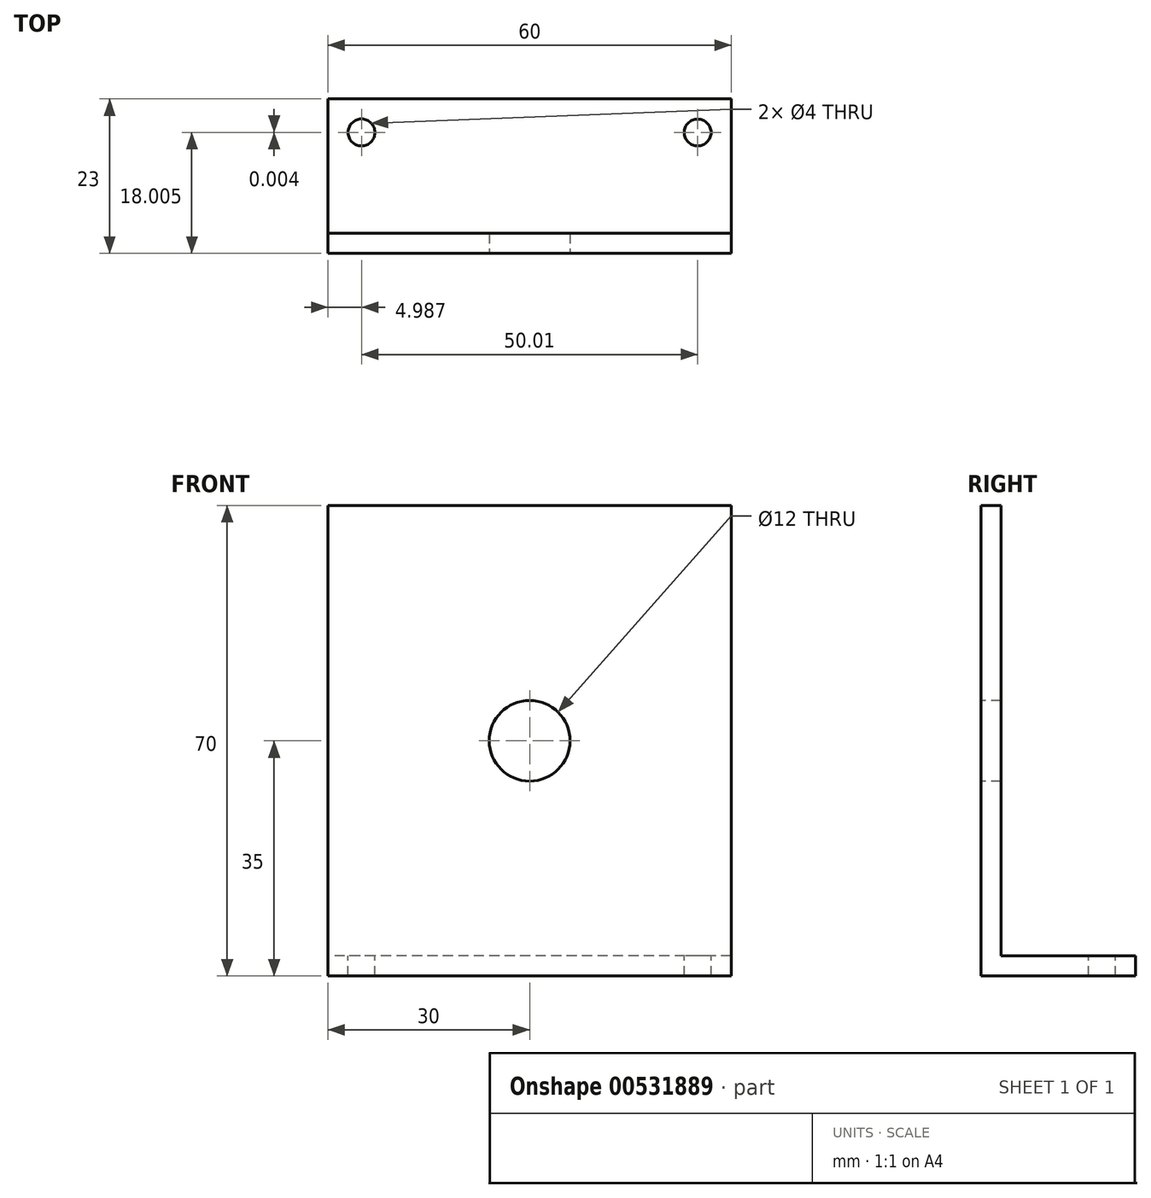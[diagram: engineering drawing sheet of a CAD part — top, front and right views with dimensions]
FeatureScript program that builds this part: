
annotation { "Feature Type Name" : "Feature", "Feature Type Description" : "" }
export const myFeature = defineFeature(function(context is Context, id is Id, definition is map)
    precondition{}
    {
        {
            var Q0;
            Q0=qCreatedBy(makeId("Front.planeOp"),FACE);
            var sketch = newSketch(context, id + "F0", { "sketchPlane" : qUnion([Q0])});
            skLineSegment(sketch, "E0.bottom", {"start": v(30, -35) * mm, "end": v(-30, -35) * mm});
            skLineSegment(sketch, "E0.top", {"start": v(30, 35) * mm, "end": v(-30, 35) * mm});
            skLineSegment(sketch, "E0.left", {"start": v(30, -35) * mm, "end": v(30, 35) * mm});
            skLineSegment(sketch, "E0.right", {"start": v(-30, -35) * mm, "end": v(-30, 35) * mm});
            skPoint(sketch, "E0.middle", {"position": v(0, 0) * mm});
            skSolve(sketch);
        }
        {
            var Q0;
            Q0=makeQuery(id+"F0.imprint","IMPRINT",FACE,{"disambiguationData":[TD([[makeQuery(id+"F0.imprint","IMPRINT",EDGE,{"derivedFrom":sQuery(id+"F0.wireOp",EDGE,"E0.bottom")}),-1.0]])]});
            extrude(context, id + "F1", {"entities" : qUnion([Q0]), "depth" : 3 * mm, "offsetDistance" : 25 * mm});
        }
        {
            var Q0;
            Q0=makeQuery(id+"F1.opExtrude","CAP_FACE",FACE,{"disambiguationData":[OSD([sQuery(id+"F0.wireOp",EDGE,"E0.bottom"),sQuery(id+"F0.wireOp",EDGE,"E0.top"),sQuery(id+"F0.wireOp",EDGE,"E0.left"),sQuery(id+"F0.wireOp",EDGE,"E0.right")])],"isStart":true});
            var sketch = newSketch(context, id + "F2", { "sketchPlane" : qUnion([Q0])});
            skLineSegment(sketch, "E1.bottom", {"start": v(-30, -35) * mm, "end": v(30, -35) * mm});
            skLineSegment(sketch, "E1.top", {"start": v(-30, -32) * mm, "end": v(30, -32) * mm});
            skLineSegment(sketch, "E1.left", {"start": v(-30, -35) * mm, "end": v(-30, -32) * mm});
            skLineSegment(sketch, "E1.right", {"start": v(30, -35) * mm, "end": v(30, -32) * mm});
            skSolve(sketch);
        }
        {
            var Q0;
            Q0 = qSketchRegion(id + "F2", true);
            extrude(context, id + "F3", {"entities" : qUnion([Q0]), "operationType" : NewBodyOperationType.ADD, "depth" : 20 * mm, "offsetDistance" : 25 * mm});
        }
        {
            var Q0;
            Q0=makeQuery(id+"F3.opExtrude","SWEPT_FACE",FACE,{"disambiguationData":[OSD([sQuery(id+"F2.wireOp",EDGE,"E1.top")])]});
            var sketch = newSketch(context, id + "F4", { "sketchPlane" : qUnion([Q0])});
            skLineSegment(sketch, "E2", {"start": v(30, 20) * mm, "end": v(30, 17.5) * mm});
            skCircle(sketch, "E3", {"center": v(25, 15) * mm, "radius": 2 * mm});
            skLineSegment(sketch, "E4", {"start": v(-30, 20) * mm, "end": v(-30, 17.5) * mm});
            skCircle(sketch, "E5", {"center": v(-25.01, 15) * mm, "radius": 2 * mm});
            skLineSegment(sketch, "E6", {"start": v(-30, 20) * mm, "end": v(-30, 15) * mm});
            skLineSegment(sketch, "E7", {"start": v(-30, 15) * mm, "end": v(-25, 15) * mm});
            skLineSegment(sketch, "E8", {"start": v(30, 20) * mm, "end": v(30, 15) * mm});
            skLineSegment(sketch, "E9", {"start": v(30, 15) * mm, "end": v(25, 15) * mm});
            skSolve(sketch);
        }
        {
            var Q0;
            Q0=makeQuery(id+"F4.imprint","IMPRINT",FACE,{"disambiguationData":[TD([[makeQuery(id+"F4.imprint","IMPRINT",EDGE,{"derivedFrom":sQuery(id+"F4.wireOp",EDGE,"E3")}),1.0]])]});
            var Q1;
            Q1=makeQuery(id+"F4.imprint","IMPRINT",FACE,{"disambiguationData":[TD([[makeQuery(id+"F4.imprint","IMPRINT",EDGE,{"derivedFrom":sQuery(id+"F4.wireOp",EDGE,"E5")}),1.0]])]});
            extrude(context, id + "F5", {"entities" : qUnion([Q0, Q1]), "operationType" : NewBodyOperationType.REMOVE, "oppositeDirection" : true, "depth" : 3 * mm, "offsetDistance" : 25 * mm});
        }
        {
            var Q0;
            Q0=makeQuery(id+"F1.opExtrude","CAP_FACE",FACE,{"disambiguationData":[OSD([sQuery(id+"F0.wireOp",EDGE,"E0.bottom"),sQuery(id+"F0.wireOp",EDGE,"E0.top"),sQuery(id+"F0.wireOp",EDGE,"E0.left"),sQuery(id+"F0.wireOp",EDGE,"E0.right")])],"isStart":false});
            var sketch = newSketch(context, id + "F6", { "sketchPlane" : qUnion([Q0])});
            skCircle(sketch, "E10", {"center": v(0, 0) * mm, "radius": 6 * mm});
            skSolve(sketch);
        }
        {
            var Q0;
            Q0=makeQuery(id+"F6.imprint","IMPRINT",FACE,{"disambiguationData":[TD([[makeQuery(id+"F6.imprint","IMPRINT",EDGE,{"derivedFrom":sQuery(id+"F6.wireOp",EDGE,"E10")}),1.0]])]});
            extrude(context, id + "F7", {"entities" : qUnion([Q0]), "operationType" : NewBodyOperationType.REMOVE, "oppositeDirection" : true, "depth" : 3 * mm, "offsetDistance" : 25 * mm});
        }
    });
